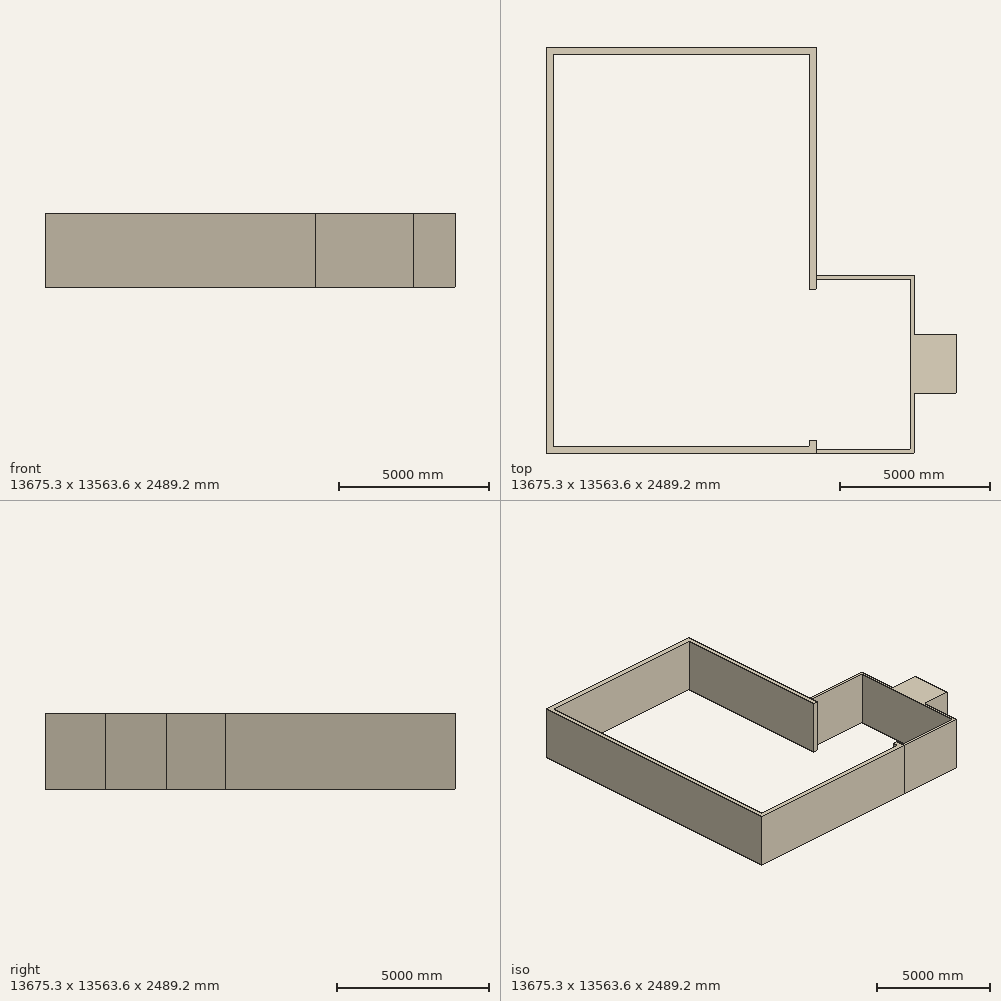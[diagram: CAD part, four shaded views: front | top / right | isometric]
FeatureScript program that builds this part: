
annotation { "Feature Type Name" : "Feature", "Feature Type Description" : "" }
export const myFeature = defineFeature(function(context is Context, id is Id, definition is map)
    precondition{}
    {
        {
            var Q0;
            Q0=qCreatedBy(makeId("Top.planeOp"),FACE);
            var sketch = newSketch(context, id + "F0", { "sketchPlane" : qUnion([Q0])});
            skLineSegment(sketch, "E0.bottom", {"start": v(-4495.8, 6781.8) * mm, "end": v(4495.8, 6781.8) * mm});
            skLineSegment(sketch, "E0.top", {"start": v(-4495.8, -6781.8) * mm, "end": v(4495.8, -6781.8) * mm});
            skLineSegment(sketch, "E0.left", {"start": v(-4495.8, 6781.8) * mm, "end": v(-4495.8, -6781.8) * mm});
            skLineSegment(sketch, "E0.right", {"start": v(4495.8, 6781.8) * mm, "end": v(4495.8, -1295.4) * mm});
            skLineSegment(sketch, "E1.0", {"start": v(-4267.2, 6553.2) * mm, "end": v(-4267.2, -6553.2) * mm});
            skLineSegment(sketch, "E1.1", {"start": v(-4267.2, 6553.2) * mm, "end": v(4267.2, 6553.2) * mm});
            skLineSegment(sketch, "E1.2", {"start": v(4267.2, 6553.2) * mm, "end": v(4267.2, -1295.4) * mm});
            skLineSegment(sketch, "E1.3", {"start": v(-4267.2, -6553.2) * mm, "end": v(4267.2, -6553.2) * mm});
            skLineSegment(sketch, "E2", {"start": v(0, 6553.2) * mm, "end": v(0, -6553.2) * mm, "construction": true});
            skLineSegment(sketch, "E3", {"start": v(-4267.2, 0) * mm, "end": v(4267.2, 0) * mm, "construction": true});
            skLineSegment(sketch, "E4", {"start": v(4267.2, -6324.6) * mm, "end": v(4495.8, -6324.6) * mm});
            skLineSegment(sketch, "E5", {"start": v(4267.2, -1295.4) * mm, "end": v(4495.8, -1295.4) * mm});
            skLineSegment(sketch, "E6.trimOffspring", {"start": v(4495.8, -6324.6) * mm, "end": v(4495.8, -6781.8) * mm});
            skLineSegment(sketch, "E7.trimOffspring", {"start": v(4267.2, -6324.6) * mm, "end": v(4267.2, -6553.2) * mm});
            skSolve(sketch);
        }
        {
            var Q0;
            Q0 = qSketchRegion(id + "F0", true);
            extrude(context, id + "F1", {"entities" : qUnion([Q0]), "depth" : 2489.2 * mm});
        }
        {
            var Q0;
            Q0=qCreatedBy(makeId("Top.planeOp"),FACE);
            var sketch = newSketch(context, id + "F2", { "sketchPlane" : qUnion([Q0])});
            skLineSegment(sketch, "E8", {"start": v(7647.55, -969.32) * mm, "end": v(7647.55, -6648.48) * mm});
            skLineSegment(sketch, "E9", {"start": v(7647.55, -6648.48) * mm, "end": v(4498.27, -6648.48) * mm});
            skLineSegment(sketch, "E10", {"start": v(4501.24, -969.32) * mm, "end": v(7647.55, -969.32) * mm});
            skLineSegment(sketch, "E11", {"start": v(7647.55, -2786.3) * mm, "end": v(9179.54, -2786.3) * mm});
            skLineSegment(sketch, "E12", {"start": v(9179.54, -2786.3) * mm, "end": v(9179.54, -4783.23) * mm});
            skLineSegment(sketch, "E13", {"start": v(9179.54, -4783.23) * mm, "end": v(7647.55, -4783.23) * mm});
            skLineSegment(sketch, "E14.0", {"start": v(7774.55, -6775.48) * mm, "end": v(4498.27, -6775.48) * mm});
            skLineSegment(sketch, "E14.1", {"start": v(7774.55, -842.32) * mm, "end": v(7774.55, -6775.48) * mm});
            skLineSegment(sketch, "E14.2", {"start": v(4501.24, -842.32) * mm, "end": v(7774.55, -842.32) * mm});
            skLineSegment(sketch, "E15", {"start": v(4501.24, -842.32) * mm, "end": v(4501.24, -969.32) * mm});
            skLineSegment(sketch, "E16", {"start": v(4498.27, -6648.48) * mm, "end": v(4498.27, -6775.48) * mm});
            skSolve(sketch);
        }
        {
            var Q0;
            Q0 = qSketchRegion(id + "F2", true);
            extrude(context, id + "F3", {"entities" : qUnion([Q0]), "depth" : 2489.2 * mm, "offsetDistance" : 25.4 * mm});
        }
    });
